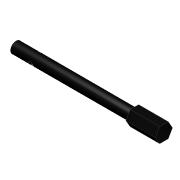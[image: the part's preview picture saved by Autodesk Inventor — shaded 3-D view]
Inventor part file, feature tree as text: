
AUTODESK INVENTOR PART (.ipt)
format: ipt  version: 2012 (Build 160160000, 160)  size: 90,112 bytes
history: native  units: in
note: dims shown in document units (in); Inventor stores cm internally (conversion verified against a paired STEP export)
features: extrude x3, sketch x3
ambient origin geometry x8: Origin, YZ Plane, XZ Plane, XY Plane, X Axis, Y Axis, Z Axis, Center Point
bodies: Solid1 (feature_tree)
feature tree (6):
  extrude  "Extrusion1"  Depth=4.0in TaperAngle=0.0deg
  extrude  "Extrusion2"  Depth=0.5in TaperAngle=0.0deg
  extrude  "Extrusion3"  Depth=1.0in TaperAngle=0.0deg
  sketch  "Sketch1"  dims[d0=0.375in d1=4.0in d2=0.0in]
  sketch  "Sketch2"  dims[d3=0.5in d4=0.5in d5=0.0in]
  sketch  "Sketch3"  dims[d6=0.192in d7=1.0in d8=0.0in d9=2.5in]
